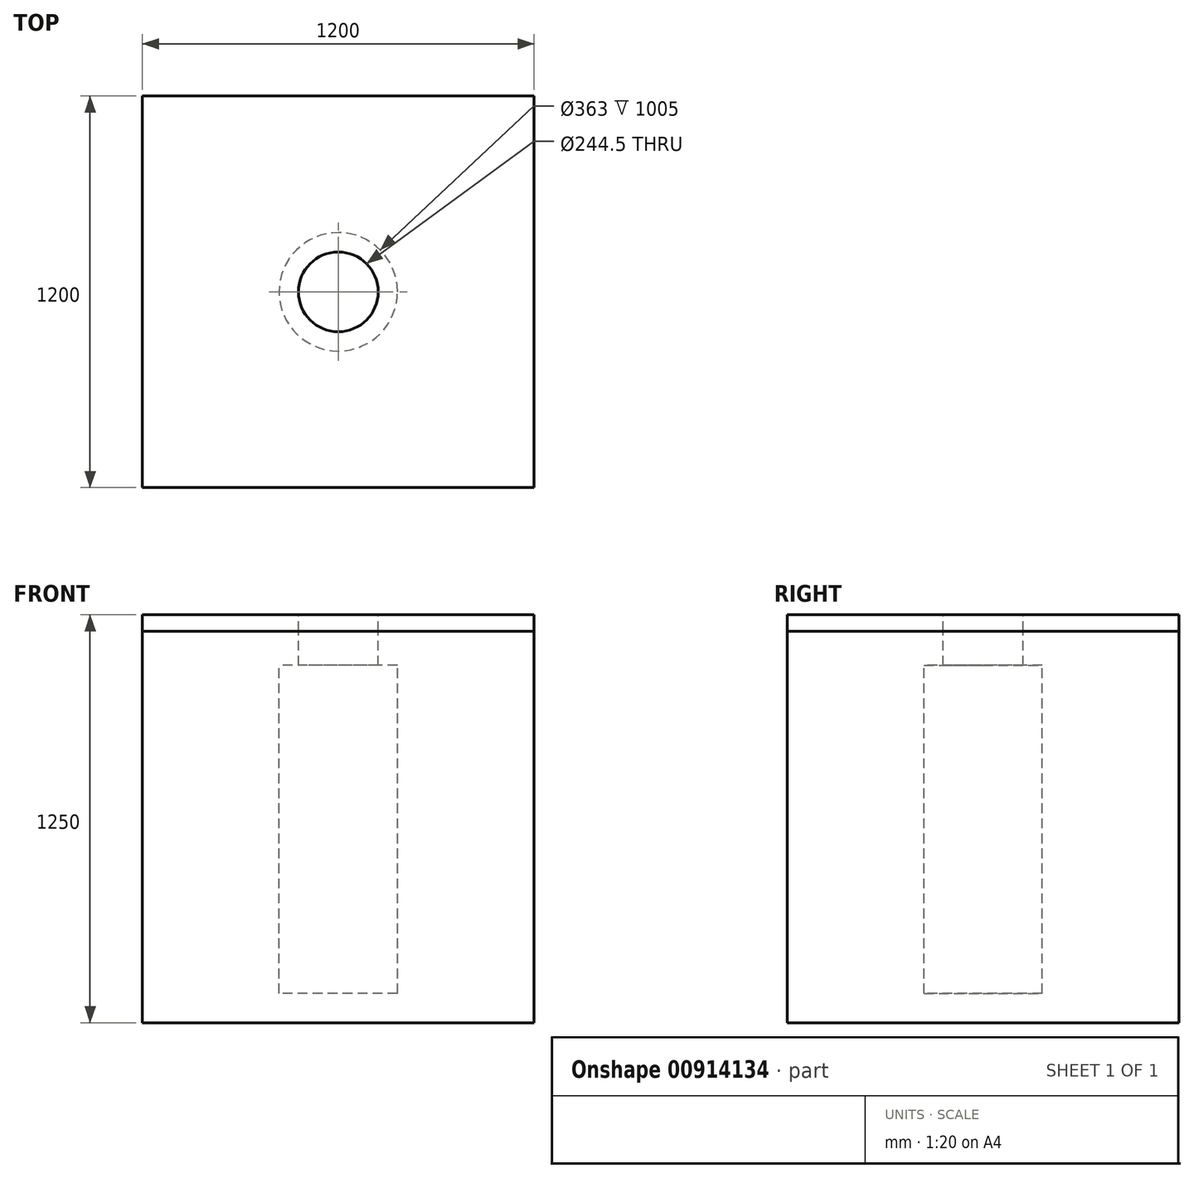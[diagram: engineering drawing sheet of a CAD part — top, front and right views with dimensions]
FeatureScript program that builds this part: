
annotation { "Feature Type Name" : "Feature", "Feature Type Description" : "" }
export const myFeature = defineFeature(function(context is Context, id is Id, definition is map)
    precondition{}
    {
        {
            var Q0;
            Q0=qCreatedBy(makeId("Top.planeOp"),FACE);
            var sketch = newSketch(context, id + "F0", { "sketchPlane" : qUnion([Q0])});
            skLineSegment(sketch, "E0.bottom", {"start": v(600, 600) * mm, "end": v(-600, 600) * mm});
            skLineSegment(sketch, "E0.top", {"start": v(600, -600) * mm, "end": v(-600, -600) * mm});
            skLineSegment(sketch, "E0.left", {"start": v(600, 600) * mm, "end": v(600, -600) * mm});
            skLineSegment(sketch, "E0.right", {"start": v(-600, 600) * mm, "end": v(-600, -600) * mm});
            skPoint(sketch, "E0.middle", {"position": v(0, 0) * mm});
            skCircle(sketch, "E1", {"center": v(0, 0) * mm, "radius": 122.25 * mm});
            skSolve(sketch);
        }
        {
            var Q0;
            Q0=makeQuery(id+"F0.imprint","IMPRINT",FACE,{"disambiguationData":[TD([[makeQuery(id+"F0.imprint","IMPRINT",EDGE,{"derivedFrom":sQuery(id+"F0.wireOp",EDGE,"E0.bottom")}),1.0]])]});
            extrude(context, id + "F1", {"entities" : qUnion([Q0]), "oppositeDirection" : true, "depth" : 50 * mm, "offsetDistance" : 25 * mm});
        }
        {
            var Q0;
            Q0=makeQuery(id+"F1.opExtrude","CAP_FACE",FACE,{"disambiguationData":[OSD([sQuery(id+"F0.wireOp",EDGE,"E0.bottom"),sQuery(id+"F0.wireOp",EDGE,"E0.top"),sQuery(id+"F0.wireOp",EDGE,"E0.left"),sQuery(id+"F0.wireOp",EDGE,"E0.right"),sQuery(id+"F0.wireOp",EDGE,"E1")])],"isStart":false});
            var sketch = newSketch(context, id + "F2", { "sketchPlane" : qUnion([Q0])});
            skLineSegment(sketch, "E2.0.0", {"start": v(600, 600) * mm, "end": v(-600, 600) * mm});
            skLineSegment(sketch, "E2.0.1", {"start": v(-600, 600) * mm, "end": v(-600, -600) * mm});
            skLineSegment(sketch, "E2.0.2", {"start": v(-600, -600) * mm, "end": v(600, -600) * mm});
            skLineSegment(sketch, "E2.0.3", {"start": v(600, -600) * mm, "end": v(600, 600) * mm});
            skSolve(sketch);
        }
        {
            var Q0;
            Q0 = qSketchRegion(id + "F2", true);
            extrude(context, id + "F3", {"entities" : qUnion([Q0]), "depth" : 1200 * mm, "offsetDistance" : 25 * mm});
        }
        {
            var Q0;
            Q0=makeQuery(id+"F3.opExtrude","CAP_FACE",FACE,{"disambiguationData":[OSD([sQuery(id+"F2.wireOp",EDGE,"E2.0.0"),sQuery(id+"F2.wireOp",EDGE,"E2.0.1"),sQuery(id+"F2.wireOp",EDGE,"E2.0.2"),sQuery(id+"F2.wireOp",EDGE,"E2.0.3")])],"isStart":true});
            var sketch = newSketch(context, id + "F4", { "sketchPlane" : qUnion([Q0])});
            skCircle(sketch, "E3.0", {"center": v(0, 0) * mm, "radius": 122.25 * mm});
            skSolve(sketch);
        }
        {
            var Q0;
            Q0 = qSketchRegion(id + "F4", true);
            extrude(context, id + "F5", {"entities" : qUnion([Q0]), "operationType" : NewBodyOperationType.REMOVE, "oppositeDirection" : true, "depth" : 105 * mm, "offsetDistance" : 25 * mm});
        }
        {
            var Q0;
            Q0=makeQuery(id+"F5.boolean.opBoolean","COPY",FACE,{"derivedFrom":makeQuery(id+"F5.opExtrude","CAP_FACE",FACE,{"disambiguationData":[OSD([sQuery(id+"F4.wireOp",EDGE,"E3.0")])],"isStart":false})});
            var sketch = newSketch(context, id + "F6", { "sketchPlane" : qUnion([Q0])});
            skCircle(sketch, "E4", {"center": v(0, 0) * mm, "radius": 181.5 * mm});
            skSolve(sketch);
        }
        {
            var Q0;
            Q0 = qSketchRegion(id + "F6", true);
            extrude(context, id + "F7", {"entities" : qUnion([Q0]), "operationType" : NewBodyOperationType.REMOVE, "oppositeDirection" : true, "depth" : 1005 * mm, "offsetDistance" : 25 * mm});
        }
    });
